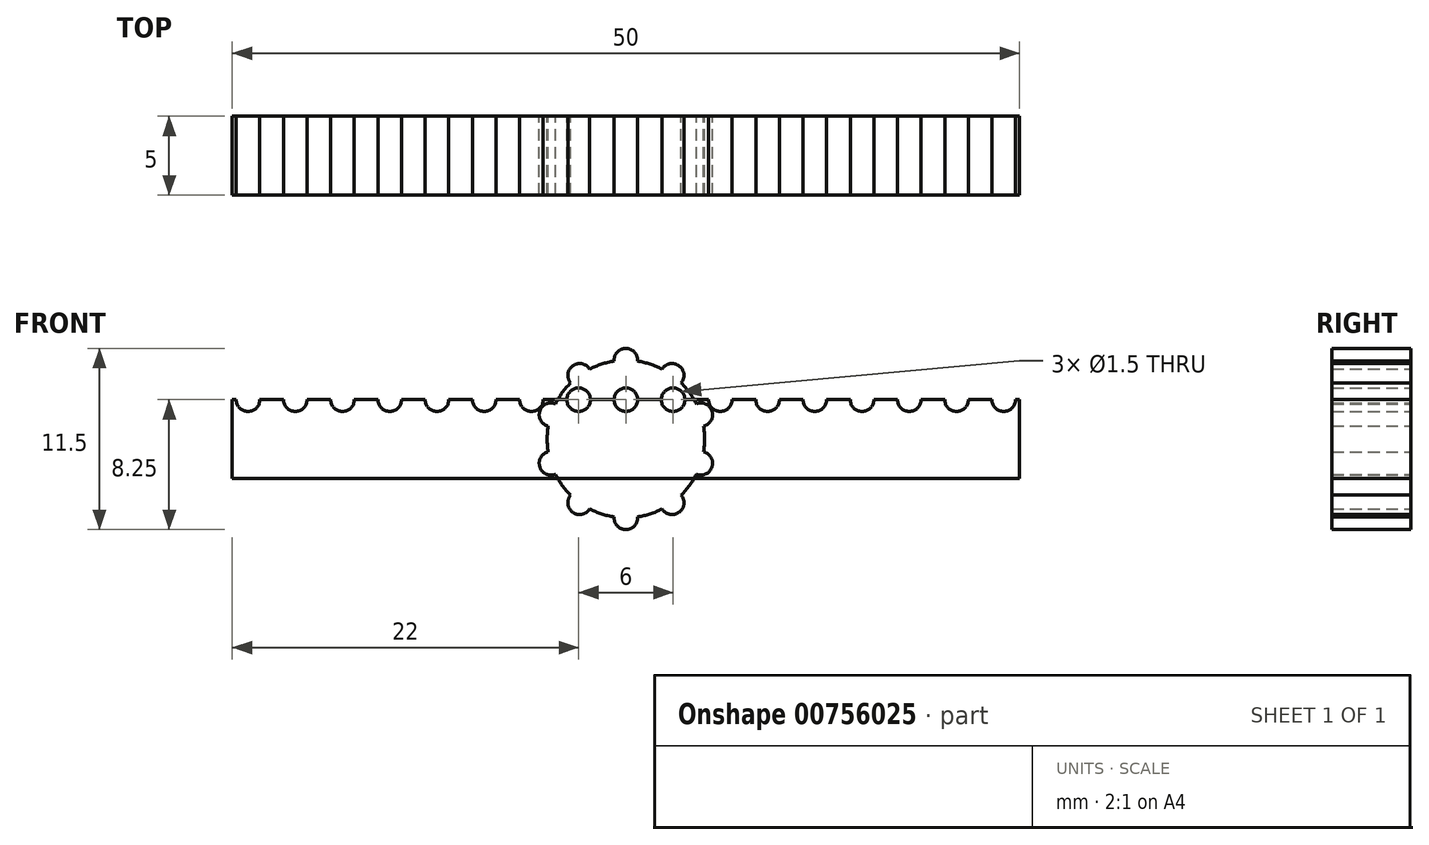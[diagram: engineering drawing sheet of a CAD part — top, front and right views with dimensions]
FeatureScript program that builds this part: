
annotation { "Feature Type Name" : "Feature", "Feature Type Description" : "" }
export const myFeature = defineFeature(function(context is Context, id is Id, definition is map)
    precondition{}
    {
        {
            var Q0;
            Q0=qCreatedBy(makeId("Front.planeOp"),FACE);
            var sketch = newSketch(context, id + "F0", { "sketchPlane" : qUnion([Q0])});
            skCircle(sketch, "E0", {"center": v(0, 0) * mm, "radius": 5 * mm});
            skSolve(sketch);
        }
        {
            var Q0;
            Q0=qCreatedBy(makeId("Front.planeOp"),FACE);
            var sketch = newSketch(context, id + "F1", { "sketchPlane" : qUnion([Q0])});
            skCircle(sketch, "E1", {"center": v(0, 5) * mm, "radius": 0.75 * mm});
            skCircle(sketch, "E2.1.0", {"center": v(-2.94, 4.05) * mm, "radius": 0.75 * mm});
            skCircle(sketch, "E2.2.0", {"center": v(-4.76, 1.55) * mm, "radius": 0.75 * mm});
            skCircle(sketch, "E2.3.0", {"center": v(-4.76, -1.55) * mm, "radius": 0.75 * mm});
            skCircle(sketch, "E2.4.0", {"center": v(-2.94, -4.05) * mm, "radius": 0.75 * mm});
            skCircle(sketch, "E2.5.0", {"center": v(0, -5) * mm, "radius": 0.75 * mm});
            skCircle(sketch, "E2.6.0", {"center": v(2.94, -4.05) * mm, "radius": 0.75 * mm});
            skCircle(sketch, "E2.7.0", {"center": v(4.76, -1.55) * mm, "radius": 0.75 * mm});
            skCircle(sketch, "E2.8.0", {"center": v(4.76, 1.55) * mm, "radius": 0.75 * mm});
            skCircle(sketch, "E2.9.0", {"center": v(2.94, 4.05) * mm, "radius": 0.75 * mm});
            skPoint(sketch, "E2.center", {"position": v(0, 0) * mm});
            skSolve(sketch);
        }
        {
            var Q0;
            Q0 = qSketchRegion(id + "F0", true);
            extrude(context, id + "F2", {"entities" : qUnion([Q0]), "depth" : 5 * mm, "offsetDistance" : 25 * mm});
        }
        {
            var Q0;
            Q0 = qSketchRegion(id + "F1", true);
            extrude(context, id + "F3", {"entities" : qUnion([Q0]), "operationType" : NewBodyOperationType.ADD, "depth" : 5 * mm, "offsetDistance" : 25 * mm});
        }
        {
            var Q0;
            Q0=qCreatedBy(makeId("Front.planeOp"),FACE);
            var sketch = newSketch(context, id + "F4", { "sketchPlane" : qUnion([Q0])});
            skLineSegment(sketch, "E3.bottom", {"start": v(25, 2.5) * mm, "end": v(-25, 2.5) * mm});
            skLineSegment(sketch, "E3.top", {"start": v(25, -2.5) * mm, "end": v(-25, -2.5) * mm});
            skLineSegment(sketch, "E3.left", {"start": v(25, 2.5) * mm, "end": v(25, -2.5) * mm});
            skLineSegment(sketch, "E3.right", {"start": v(-25, 2.5) * mm, "end": v(-25, -2.5) * mm});
            skPoint(sketch, "E3.middle", {"position": v(0, 0) * mm});
            skSolve(sketch);
        }
        {
            var Q0;
            Q0 = qSketchRegion(id + "F4", true);
            extrude(context, id + "F5", {"entities" : qUnion([Q0]), "depth" : 5 * mm, "offsetDistance" : 25 * mm});
        }
        {
            var Q0;
            Q0=qCreatedBy(makeId("Front.planeOp"),FACE);
            var sketch = newSketch(context, id + "F6", { "sketchPlane" : qUnion([Q0])});
            skCircle(sketch, "E4", {"center": v(-24, 2.5) * mm, "radius": 0.75 * mm});
            skCircle(sketch, "E5.1.0.0", {"center": v(-21, 2.5) * mm, "radius": 0.75 * mm});
            skCircle(sketch, "E5.2.0.0", {"center": v(-18, 2.5) * mm, "radius": 0.75 * mm});
            skCircle(sketch, "E5.3.0.0", {"center": v(-15, 2.5) * mm, "radius": 0.75 * mm});
            skCircle(sketch, "E5.4.0.0", {"center": v(-12, 2.5) * mm, "radius": 0.75 * mm});
            skCircle(sketch, "E5.5.0.0", {"center": v(-9, 2.5) * mm, "radius": 0.75 * mm});
            skCircle(sketch, "E5.6.0.0", {"center": v(-6, 2.5) * mm, "radius": 0.75 * mm});
            skCircle(sketch, "E5.7.0.0", {"center": v(-3, 2.5) * mm, "radius": 0.75 * mm});
            skCircle(sketch, "E5.8.0.0", {"center": v(0, 2.5) * mm, "radius": 0.75 * mm});
            skCircle(sketch, "E5.9.0.0", {"center": v(3, 2.5) * mm, "radius": 0.75 * mm});
            skCircle(sketch, "E5.10.0.0", {"center": v(6, 2.5) * mm, "radius": 0.75 * mm});
            skCircle(sketch, "E5.11.0.0", {"center": v(9, 2.5) * mm, "radius": 0.75 * mm});
            skLineSegment(sketch, "E5.direction1", {"start": v(-24, 2.5) * mm, "end": v(-21, 2.5) * mm, "construction": true});
            skCircle(sketch, "E6.0.12.0", {"center": v(12, 2.5) * mm, "radius": 0.75 * mm});
            skCircle(sketch, "E6.0.13.0", {"center": v(15, 2.5) * mm, "radius": 0.75 * mm});
            skCircle(sketch, "E7.0.14.0", {"center": v(18, 2.5) * mm, "radius": 0.75 * mm});
            skCircle(sketch, "E7.0.15.0", {"center": v(21, 2.5) * mm, "radius": 0.75 * mm});
            skCircle(sketch, "E7.0.16.0", {"center": v(24, 2.5) * mm, "radius": 0.75 * mm});
            skSolve(sketch);
        }
        {
            var Q0;
            Q0 = qSketchRegion(id + "F6", true);
            extrude(context, id + "F7", {"entities" : qUnion([Q0]), "operationType" : NewBodyOperationType.REMOVE, "depth" : 5 * mm, "offsetDistance" : 25 * mm});
        }
    });
